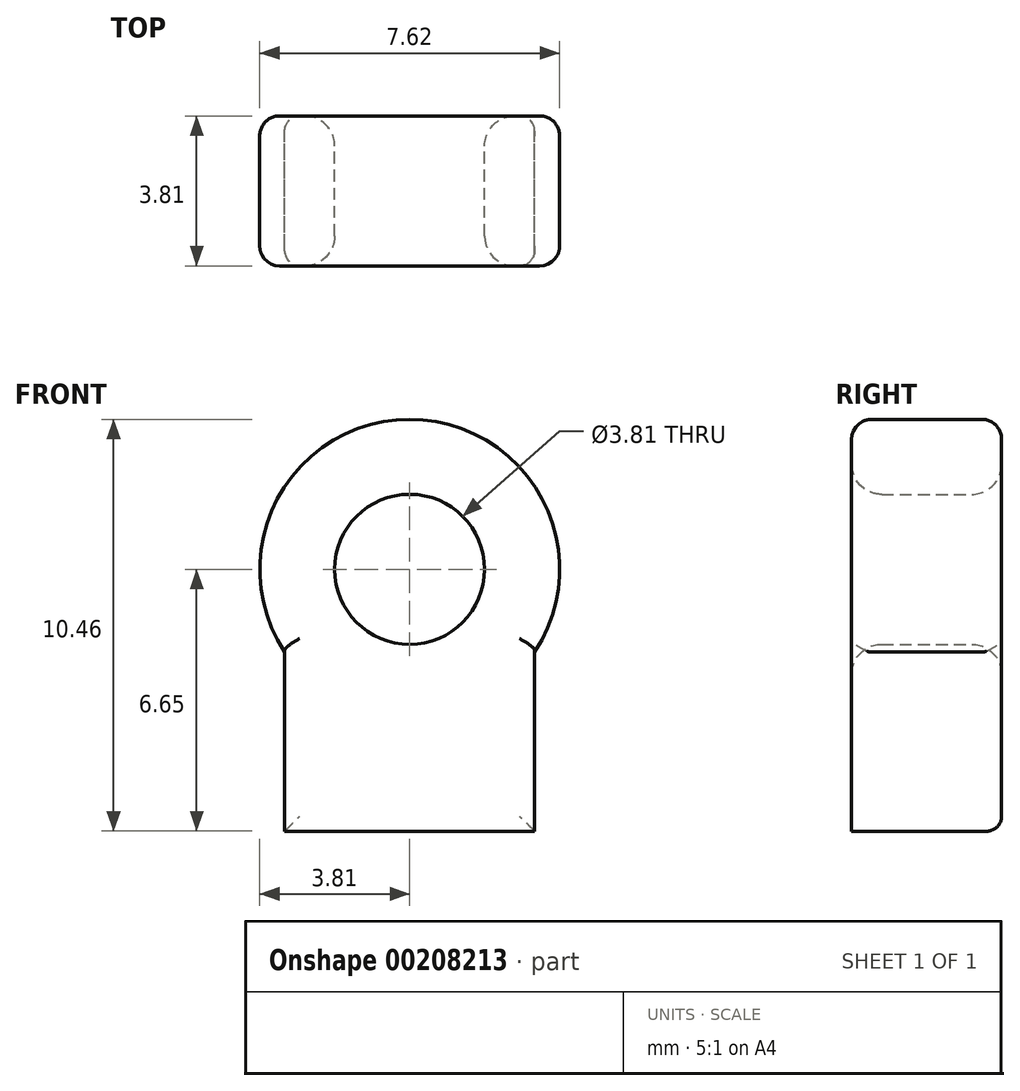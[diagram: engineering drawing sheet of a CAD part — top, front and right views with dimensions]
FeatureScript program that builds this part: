
annotation { "Feature Type Name" : "Feature", "Feature Type Description" : "" }
export const myFeature = defineFeature(function(context is Context, id is Id, definition is map)
    precondition{}
    {
        {
            var Q0;
            Q0=qCreatedBy(makeId("Front.planeOp"),FACE);
            var sketch = newSketch(context, id + "F2", { "sketchPlane" : qUnion([Q0])});
            skArc(sketch, "E0", {"start": v(3.18, -2.1) * mm, "mid": v(0, 3.81) * mm, "end": v(-3.18, -2.1) * mm});
            skCircle(sketch, "E1", {"center": v(0, 0) * mm, "radius": 1.9 * mm});
            skLineSegment(sketch, "E2", {"start": v(0, 0) * mm, "end": v(0, -6.65) * mm});
            skLineSegment(sketch, "E3.0", {"start": v(-3.18, -2.1) * mm, "end": v(-3.18, -6.65) * mm});
            skLineSegment(sketch, "E4.0", {"start": v(3.17, -2.1) * mm, "end": v(3.18, -6.65) * mm});
            skLineSegment(sketch, "E5", {"start": v(-3.18, -6.65) * mm, "end": v(3.18, -6.65) * mm});
            skSolve(sketch);
        }
        {
            var Q0;
            Q0=makeQuery(id+"F2.imprint","IMPRINT",FACE,{"disambiguationData":[TD([[makeQuery(id+"F2.imprint","IMPRINT",EDGE,{"derivedFrom":sQuery(id+"F2.wireOp",EDGE,"E0")}),1.0]])]});
            extrude(context, id + "F0", {"entities" : qUnion([Q0]), "depth" : 3.8 * mm});
        }
        {
            var Q0;
            Q0=makeQuery(id+"F0.opExtrude","CAP_EDGE",EDGE,{"disambiguationData":[OSD([sQuery(id+"F2.wireOp",EDGE,"E1")])],"isStart":false});
            var Q1;
            Q1=makeQuery(id+"F0.opExtrude","CAP_EDGE",EDGE,{"disambiguationData":[OSD([sQuery(id+"F2.wireOp",EDGE,"E1")])],"isStart":true});
            fillet(context, id + "F3", {"entities" : qUnion([Q0, Q1]), "radius" : 0.76 * mm, "tangentPropagation" : true, "allowEdgeOverflow" : false});
        }
        {
            var Q0;
            Q0=makeQuery(id+"F0.opExtrude","CAP_EDGE",EDGE,{"disambiguationData":[OSD([sQuery(id+"F2.wireOp",EDGE,"E0")])],"isStart":true});
            var Q1;
            Q1=makeQuery(id+"F0.opExtrude","CAP_EDGE",EDGE,{"disambiguationData":[OSD([sQuery(id+"F2.wireOp",EDGE,"E0")])],"isStart":false});
            fillet(context, id + "F1", {"entities" : qUnion([Q0, Q1]), "radius" : 0.5 * mm, "tangentPropagation" : true, "allowEdgeOverflow" : false});
        }
        {
            var Q0;
            Q0=makeQuery(id+"F0.opExtrude","CAP_EDGE",EDGE,{"disambiguationData":[OSD([sQuery(id+"F2.wireOp",EDGE,"E3.0")])],"isStart":true});
            var Q1;
            Q1=makeQuery(id+"F0.opExtrude","CAP_EDGE",EDGE,{"disambiguationData":[OSD([sQuery(id+"F2.wireOp",EDGE,"E3.0")])],"isStart":false});
            var Q2;
            Q2=makeQuery(id+"F0.opExtrude","CAP_EDGE",EDGE,{"disambiguationData":[OSD([sQuery(id+"F2.wireOp",EDGE,"E4.0")])],"isStart":false});
            var Q3;
            Q3=makeQuery(id+"F0.opExtrude","CAP_FACE",FACE,{"disambiguationData":[OSD([sQuery(id+"F2.wireOp",EDGE,"E0"),sQuery(id+"F2.wireOp",EDGE,"E1"),sQuery(id+"F2.wireOp",EDGE,"E3.0"),sQuery(id+"F2.wireOp",EDGE,"E4.0"),sQuery(id+"F2.wireOp",EDGE,"E5")])],"isStart":true});
            fillet(context, id + "F4", {"entities" : qUnion([Q0, Q1, Q2, Q3]), "radius" : 0.38 * mm, "tangentPropagation" : true, "allowEdgeOverflow" : false});
        }
    });
